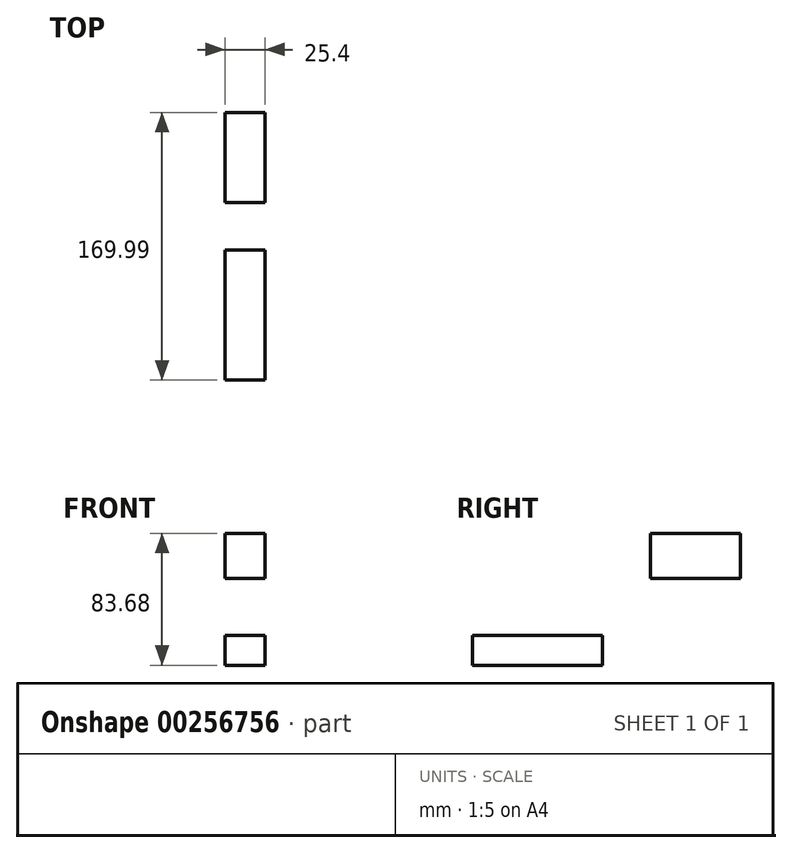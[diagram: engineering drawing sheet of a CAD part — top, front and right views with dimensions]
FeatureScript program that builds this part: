
annotation { "Feature Type Name" : "Feature", "Feature Type Description" : "" }
export const myFeature = defineFeature(function(context is Context, id is Id, definition is map)
    precondition{}
    {
        {
            var Q0;
            Q0=qCreatedBy(makeId("Right.planeOp"),FACE);
            var sketch = newSketch(context, id + "F0", { "sketchPlane" : qUnion([Q0])});
            skLineSegment(sketch, "E0.bottom", {"start": v(44.9, 3.8) * mm, "end": v(-37.65, 3.8) * mm});
            skLineSegment(sketch, "E0.top", {"start": v(44.9, -15.26) * mm, "end": v(-37.65, -15.26) * mm});
            skLineSegment(sketch, "E0.left", {"start": v(44.9, 3.8) * mm, "end": v(44.9, -15.26) * mm});
            skLineSegment(sketch, "E0.right", {"start": v(-37.65, 3.8) * mm, "end": v(-37.65, -15.26) * mm});
            skPoint(sketch, "E0.middle", {"position": v(3.62, -5.73) * mm});
            skLineSegment(sketch, "E1", {"start": v(44.9, 3.8) * mm, "end": v(44.9, 40.32) * mm});
            skArc(sketch, "E2", {"start": v(44.9, 40.32) * mm, "mid": v(45.78, 45.35) * mm, "end": v(48.32, 49.78) * mm});
            skLineSegment(sketch, "E3.bottom", {"start": v(132.34, 68.42) * mm, "end": v(75.13, 68.42) * mm});
            skLineSegment(sketch, "E3.top", {"start": v(132.34, 39.84) * mm, "end": v(75.13, 39.84) * mm});
            skLineSegment(sketch, "E3.left", {"start": v(132.34, 68.42) * mm, "end": v(132.34, 39.84) * mm});
            skLineSegment(sketch, "E3.right", {"start": v(75.13, 68.42) * mm, "end": v(75.13, 39.84) * mm});
            skPoint(sketch, "E3.middle", {"position": v(103.74, 54.13) * mm});
            skLineSegment(sketch, "E4", {"start": v(48.32, 49.78) * mm, "end": v(89.95, 49.78) * mm});
            skSolve(sketch);
        }
        {
            var Q0;
            Q0=makeQuery(id+"F0.imprint","IMPRINT",FACE,{"disambiguationData":[TD([[makeQuery(id+"F0.imprint","IMPRINT",EDGE,{"derivedFrom":sQuery(id+"F0.wireOp",EDGE,"E0.bottom")}),1.0]])]});
            var Q1;
            {var subQ0=sQuery(id+"F0.wireOp",EDGE,"E3.bottom");Q1=makeQuery(id+"F0.imprint","IMPRINT",FACE,{"disambiguationData":[TD([[makeQuery(id+"F0.imprint","IMPRINT",EDGE,{"derivedFrom":subQ0}),1.0]])]});}
            extrude(context, id + "F1", {"entities" : qUnion([Q0, Q1]), "oppositeDirection" : true, "depth" : 25.4 * mm});
        }
        {
            var Q0;
            Q0=sQuery(id+"F0.wireOp",EDGE,"E2");
            var Q1;
            Q1=sQuery(id+"F0.wireOp",EDGE,"E1");
            var Q2;
            Q2=sQuery(id+"F0.wireOp",EDGE,"E4");
            extrude(context, id + "F2", {"bodyType" : ToolBodyType.SURFACE, "surfaceEntities" : qUnion([Q0, Q1, Q2]), "oppositeDirection" : true, "depth" : 25.65 * mm});
        }
    });
